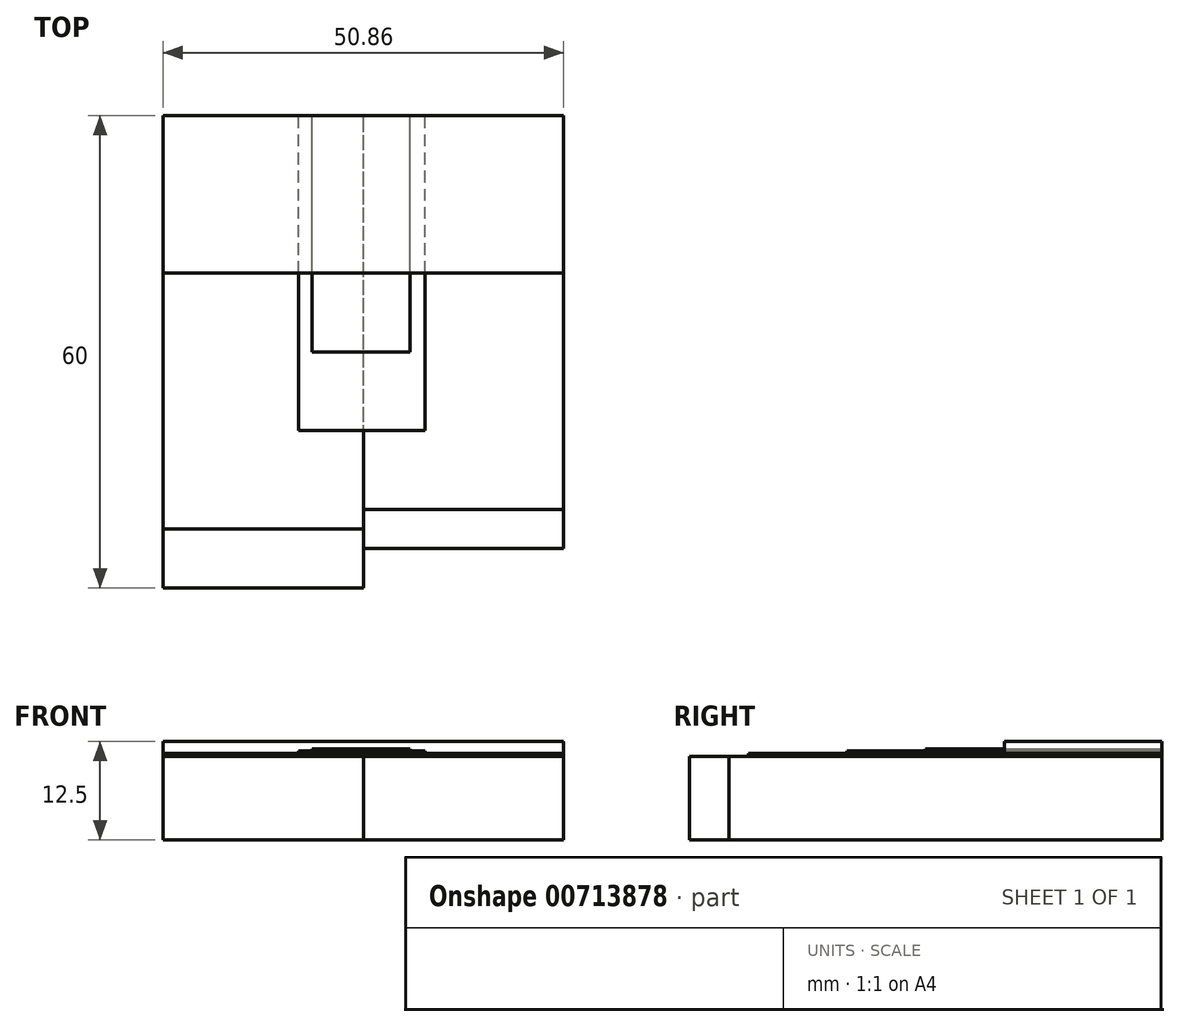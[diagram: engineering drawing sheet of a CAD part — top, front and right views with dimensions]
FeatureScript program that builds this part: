
annotation { "Feature Type Name" : "Feature", "Feature Type Description" : "" }
export const myFeature = defineFeature(function(context is Context, id is Id, definition is map)
    precondition{}
    {
        {
            var Q0;
            Q0=qCreatedBy(makeId("Front.planeOp"),FACE);
            var sketch = newSketch(context, id + "F0", { "sketchPlane" : qUnion([Q0])});
            skLineSegment(sketch, "E0.bottom", {"start": v(-37.48, 13.47) * mm, "end": v(13.38, 13.47) * mm});
            skLineSegment(sketch, "E0.top", {"start": v(-37.48, 2.48) * mm, "end": v(13.38, 2.48) * mm});
            skLineSegment(sketch, "E0.left", {"start": v(-37.48, 13.47) * mm, "end": v(-37.48, 2.48) * mm});
            skLineSegment(sketch, "E0.right", {"start": v(13.38, 13.47) * mm, "end": v(13.38, 2.48) * mm});
            skLineSegment(sketch, "E1", {"start": v(-12.05, 13.47) * mm, "end": v(-12.05, 2.48) * mm});
            skLineSegment(sketch, "E2", {"start": v(-20.3, 13.47) * mm, "end": v(-20.3, 13.78) * mm});
            skLineSegment(sketch, "E3", {"start": v(-20.3, 13.78) * mm, "end": v(-4.2, 13.78) * mm});
            skLineSegment(sketch, "E4", {"start": v(-4.2, 13.78) * mm, "end": v(-4.2, 13.47) * mm});
            skLineSegment(sketch, "E5", {"start": v(-18.56, 13.78) * mm, "end": v(-18.56, 14.02) * mm});
            skLineSegment(sketch, "E6", {"start": v(-18.56, 14.02) * mm, "end": v(-6.11, 14.02) * mm});
            skLineSegment(sketch, "E7", {"start": v(-6.11, 14.02) * mm, "end": v(-6.11, 13.78) * mm});
            skLineSegment(sketch, "E8", {"start": v(-37.48, 13.47) * mm, "end": v(-37.48, 14.98) * mm});
            skLineSegment(sketch, "E9", {"start": v(-37.48, 14.98) * mm, "end": v(13.38, 14.98) * mm});
            skLineSegment(sketch, "E10", {"start": v(13.38, 14.98) * mm, "end": v(13.38, 13.47) * mm});
            skLineSegment(sketch, "E11", {"start": v(-37.48, 13.1) * mm, "end": v(-12.05, 13.1) * mm});
            skLineSegment(sketch, "E12", {"start": v(-12.05, 13.1) * mm, "end": v(13.38, 13.1) * mm});
            skSolve(sketch);
        }
        {
            var Q0;
            {var subQ5=sQuery(id+"F0.wireOp",EDGE,"E11");Q0=makeQuery(id+"F0.imprint","IMPRINT",FACE,{"disambiguationData":[TD([[makeQuery(id+"F0.imprint","IMPRINT",EDGE,{"derivedFrom":subQ5}),-1.0]])]});}
            extrude(context, id + "F1", {"entities" : qUnion([Q0]), "depth" : 60 * mm});
        }
        {
            var Q0;
            {var subQ5=sQuery(id+"F0.wireOp",EDGE,"E12");Q0=makeQuery(id+"F0.imprint","IMPRINT",FACE,{"disambiguationData":[TD([[makeQuery(id+"F0.imprint","IMPRINT",EDGE,{"derivedFrom":subQ5}),-1.0]])]});}
            extrude(context, id + "F2", {"entities" : qUnion([Q0]), "depth" : 55 * mm});
        }
        {
            var Q0;
            {var subQ3=sQuery(id+"F0.wireOp",EDGE,"E12");Q0=makeQuery(id+"F0.imprint","IMPRINT",FACE,{"disambiguationData":[TD([[makeQuery(id+"F0.imprint","IMPRINT",EDGE,{"derivedFrom":subQ3}),1.0]])]});}
            extrude(context, id + "F3", {"entities" : qUnion([Q0]), "depth" : 50 * mm});
        }
        {
            var Q0;
            {var subQ3=sQuery(id+"F0.wireOp",EDGE,"E11");Q0=makeQuery(id+"F0.imprint","IMPRINT",FACE,{"disambiguationData":[TD([[makeQuery(id+"F0.imprint","IMPRINT",EDGE,{"derivedFrom":subQ3}),1.0]])]});}
            extrude(context, id + "F4", {"entities" : qUnion([Q0]), "depth" : 52.5 * mm});
        }
        {
            var Q0;
            {var subQ1=sQuery(id+"F0.wireOp",EDGE,"E2");Q0=makeQuery(id+"F0.imprint","IMPRINT",FACE,{"disambiguationData":[TD([[makeQuery(id+"F0.imprint","IMPRINT",EDGE,{"derivedFrom":subQ1}),-1.0]])]});}
            extrude(context, id + "F5", {"entities" : qUnion([Q0]), "depth" : 40 * mm});
        }
        {
            var Q0;
            {var subQ0=sQuery(id+"F0.wireOp",EDGE,"E5");Q0=makeQuery(id+"F0.imprint","IMPRINT",FACE,{"disambiguationData":[TD([[makeQuery(id+"F0.imprint","IMPRINT",EDGE,{"derivedFrom":subQ0}),-1.0]])]});}
            extrude(context, id + "F6", {"entities" : qUnion([Q0]), "depth" : 30 * mm});
        }
        {
            var Q0;
            {var subQ6=sQuery(id+"F0.wireOp",EDGE,"E2");Q0=makeQuery(id+"F0.imprint","IMPRINT",FACE,{"disambiguationData":[TD([[makeQuery(id+"F0.imprint","IMPRINT",EDGE,{"derivedFrom":subQ6}),1.0]])]});}
            extrude(context, id + "F7", {"entities" : qUnion([Q0]), "depth" : 20 * mm});
        }
    });
